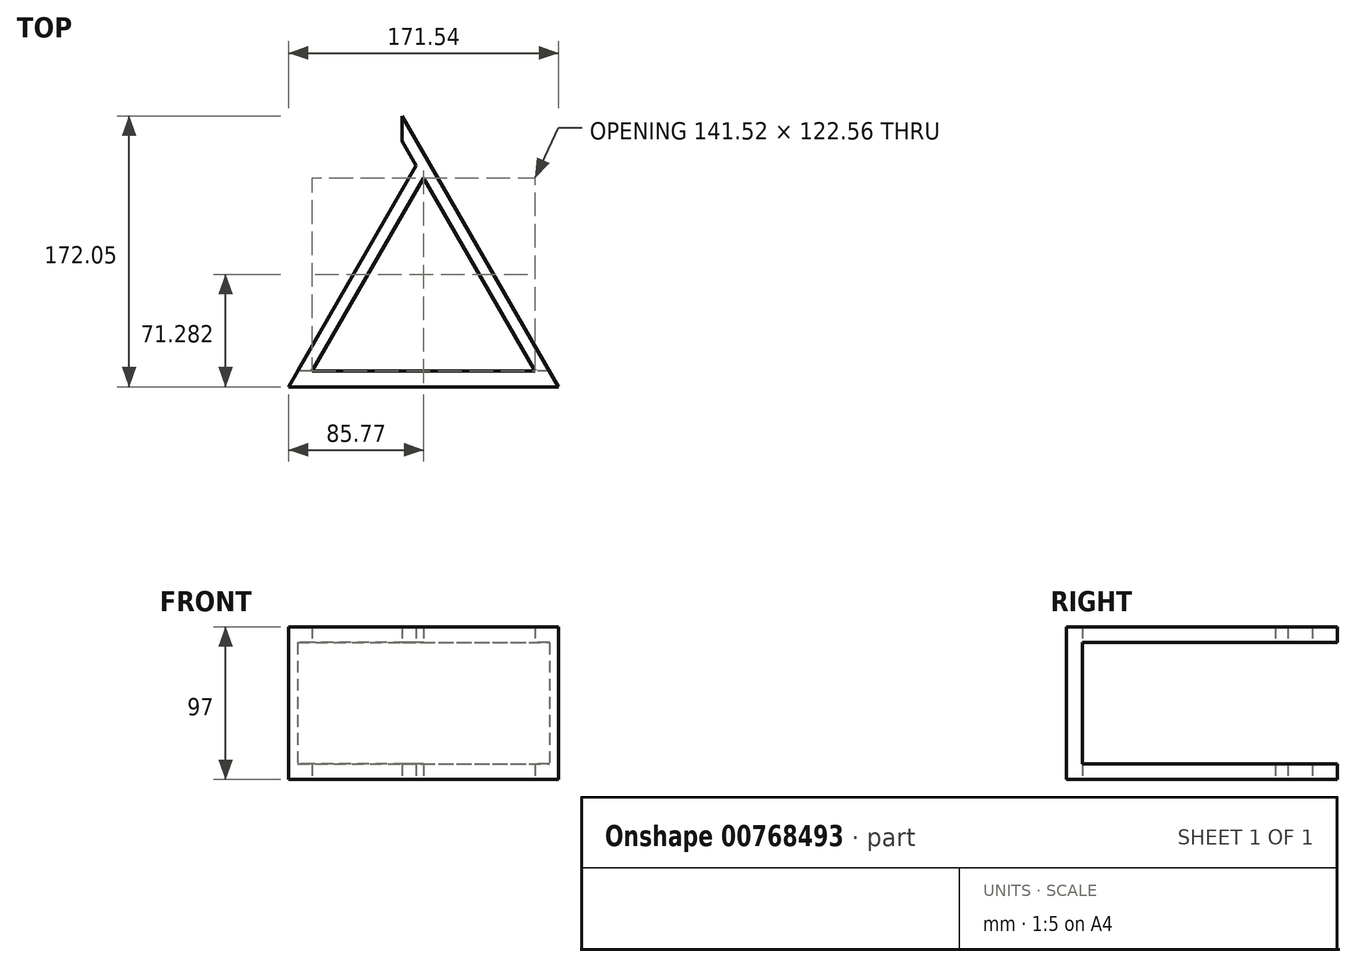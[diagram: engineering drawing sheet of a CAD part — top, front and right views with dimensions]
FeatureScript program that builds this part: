
annotation { "Feature Type Name" : "Feature", "Feature Type Description" : "" }
export const myFeature = defineFeature(function(context is Context, id is Id, definition is map)
    precondition{}
    {
        {
            var Q0;
            Q0=qCreatedBy(makeId("Top.planeOp"),FACE);
            var sketch = newSketch(context, id + "F0", { "sketchPlane" : qUnion([Q0])});
            skLineSegment(sketch, "E0.0", {"start": v(-80, -24) * mm, "end": v(-4.62, 106.56) * mm});
            skLineSegment(sketch, "E0.1", {"start": v(0, 114.56) * mm, "end": v(80, -24) * mm});
            skLineSegment(sketch, "E0.2", {"start": v(80, -24) * mm, "end": v(-80, -24) * mm});
            skPoint(sketch, "E0.0.midPoint", {"position": v(-40, 45.28) * mm});
            skPoint(sketch, "E1.end.orphan", {"position": v(90.4, 0) * mm});
            skPoint(sketch, "E2.start.orphan", {"position": v(-90.4, 0) * mm});
            skPoint(sketch, "E3.end.orphan", {"position": v(0, 126.56) * mm});
            skLineSegment(sketch, "E4", {"start": v(0, 98.56) * mm, "end": v(66.14, -16) * mm});
            skLineSegment(sketch, "E5", {"start": v(-66.14, -16) * mm, "end": v(0, 98.56) * mm});
            skLineSegment(sketch, "E6", {"start": v(-4.62, 106.56) * mm, "end": v(-13.56, 122.05) * mm});
            skLineSegment(sketch, "E7", {"start": v(0, 114.56) * mm, "end": v(-13.56, 138.05) * mm});
            skLineSegment(sketch, "E8", {"start": v(-13.56, 138.05) * mm, "end": v(-13.56, 122.05) * mm});
            skLineSegment(sketch, "E9", {"start": v(-85.77, -34) * mm, "end": v(85.77, -34) * mm});
            skLineSegment(sketch, "E10", {"start": v(-80, -24) * mm, "end": v(-85.77, -34) * mm});
            skLineSegment(sketch, "E11", {"start": v(80, -24) * mm, "end": v(85.77, -34) * mm});
            skLineSegment(sketch, "E12", {"start": v(66.14, -16) * mm, "end": v(70.76, -24) * mm});
            skLineSegment(sketch, "E13", {"start": v(-66.14, -16) * mm, "end": v(-70.76, -24) * mm});
            skSolve(sketch);
        }
        {
            var Q0;
            {var subQ0=sQuery(id+"F0.wireOp",EDGE,"E0.0");Q0=makeQuery(id+"F0.imprint","IMPRINT",FACE,{"disambiguationData":[TD([[makeQuery(id+"F0.imprint","IMPRINT",EDGE,{"derivedFrom":subQ0}),-1.0]])]});}
            var Q1;
            Q1=makeQuery(id+"F0.imprint","IMPRINT",FACE,{"disambiguationData":[TD([[makeQuery(id+"F0.imprint","IMPRINT",EDGE,{"derivedFrom":sQuery(id+"F0.wireOp",EDGE,"E9")}),1.0]])]});
            extrude(context, id + "F1", {"entities" : qUnion([Q0, Q1]), "depth" : 97 * mm, "offsetDistance" : 25 * mm});
        }
        {
            var Q0;
            {var subQ0=sQuery(id+"F0.wireOp",EDGE,"E0.0");Q0=makeQuery(id+"F0.imprint","IMPRINT",FACE,{"disambiguationData":[TD([[makeQuery(id+"F0.imprint","IMPRINT",EDGE,{"derivedFrom":subQ0}),-1.0]])]});}
            extrude(context, id + "F2", {"entities" : qUnion([Q0]), "operationType" : NewBodyOperationType.REMOVE, "depth" : 87 * mm, "offsetDistance" : 25 * mm});
        }
        {
            var Q0;
            {var subQ0=sQuery(id+"F0.wireOp",EDGE,"E0.0");Q0=makeQuery(id+"F0.imprint","IMPRINT",FACE,{"disambiguationData":[TD([[makeQuery(id+"F0.imprint","IMPRINT",EDGE,{"derivedFrom":subQ0}),-1.0]])]});}
            extrude(context, id + "F3", {"entities" : qUnion([Q0]), "operationType" : NewBodyOperationType.ADD, "depth" : 10 * mm, "offsetDistance" : 25 * mm});
        }
    });
